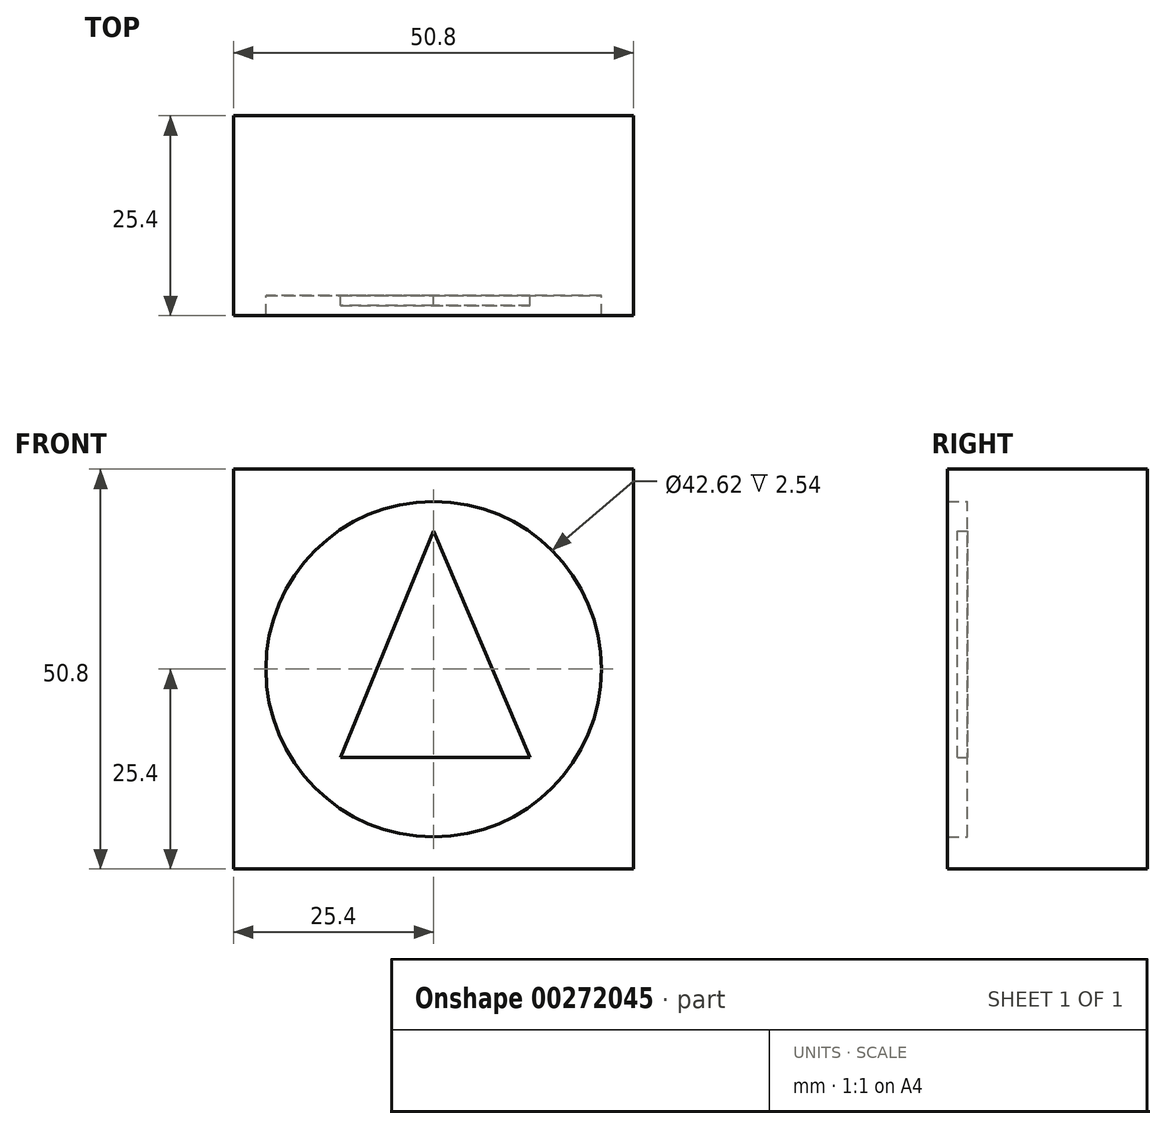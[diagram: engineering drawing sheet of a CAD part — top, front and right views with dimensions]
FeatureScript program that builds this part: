
annotation { "Feature Type Name" : "Feature", "Feature Type Description" : "" }
export const myFeature = defineFeature(function(context is Context, id is Id, definition is map)
    precondition{}
    {
        {
            var Q0;
            Q0=qCreatedBy(makeId("Front.planeOp"),FACE);
            var sketch = newSketch(context, id + "F0", { "sketchPlane" : qUnion([Q0])});
            skLineSegment(sketch, "E0.bottom", {"start": v(0, 0) * mm, "end": v(50.8, 0) * mm});
            skLineSegment(sketch, "E0.top", {"start": v(0, 50.8) * mm, "end": v(50.8, 50.8) * mm});
            skLineSegment(sketch, "E0.left", {"start": v(0, 0) * mm, "end": v(0, 50.8) * mm});
            skLineSegment(sketch, "E0.right", {"start": v(50.8, 0) * mm, "end": v(50.8, 50.8) * mm});
            skCircle(sketch, "E1", {"center": v(25.4, 25.4) * mm, "radius": 21.3 * mm});
            skLineSegment(sketch, "E2", {"start": v(25.4, 42.94) * mm, "end": v(13.57, 14.18) * mm});
            skLineSegment(sketch, "E3", {"start": v(13.57, 14.18) * mm, "end": v(37.68, 14.18) * mm});
            skLineSegment(sketch, "E4", {"start": v(37.68, 14.18) * mm, "end": v(25.4, 42.94) * mm});
            skSolve(sketch);
        }
        {
            var Q0;
            Q0=makeQuery(id+"F0.imprint","IMPRINT",FACE,{"disambiguationData":[TD([[makeQuery(id+"F0.imprint","IMPRINT",EDGE,{"derivedFrom":sQuery(id+"F0.wireOp",EDGE,"E0.bottom")}),1.0]])]});
            extrude(context, id + "F1", {"entities" : qUnion([Q0]), "depth" : 25.4 * mm});
        }
        {
            var Q0;
            Q0=makeQuery(id+"F0.imprint","IMPRINT",FACE,{"disambiguationData":[TD([[makeQuery(id+"F0.imprint","IMPRINT",EDGE,{"derivedFrom":sQuery(id+"F0.wireOp",EDGE,"E1")}),1.0]])]});
            extrude(context, id + "F2", {"entities" : qUnion([Q0]), "operationType" : NewBodyOperationType.ADD, "depth" : 22.86 * mm});
        }
        {
            var Q0;
            Q0=makeQuery(id+"F0.imprint","IMPRINT",FACE,{"disambiguationData":[TD([[makeQuery(id+"F0.imprint","IMPRINT",EDGE,{"derivedFrom":sQuery(id+"F0.wireOp",EDGE,"E2")}),1.0]])]});
            extrude(context, id + "F3", {"entities" : qUnion([Q0]), "operationType" : NewBodyOperationType.ADD, "depth" : 24.13 * mm});
        }
    });
